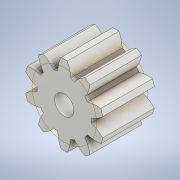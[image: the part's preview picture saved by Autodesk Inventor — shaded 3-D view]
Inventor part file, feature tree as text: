
AUTODESK INVENTOR PART (.ipt)
format: ipt  version: 2021 (Build 250183000, 183)  size: 220,160 bytes
history: native  units: mm (DEFAULTED — no unit token found)
features: plane x3, other x3, sketch x3, extrude x1, hole x1
ambient origin geometry x8: Origin, YZ Plane, XZ Plane, XY Plane, X Axis, Y Axis, Z Axis, Center Point
bodies: Solid1 (feature_tree)
feature tree (11):
  extrude  "Extrusion1"  Depth=8.0mm TaperAngle=0.0deg
  plane  "Work Plane2"
  plane  "Work Plane8"
  plane  "Work Plane9"
  other  "Spur Gear"
  hole  "Hole1"  [1 undecoded]
  sketch  "Sketch1"  dims[d0=12.303391mm d1=8.0mm d2=0.0mm]
  sketch  "Sketch2"  dims[d3=10.0mm d4=10.0mm d5=0.0mm]
  other  "Srf1"
  sketch  "Sketch3"  dims[d16=25.351695mm d17=0.0mm d34=3.141593mm d39=0.0mm d41=0.0mm d43=25.351695mm d46=25.351695mm d47=0.0mm d48=0.0mm d49=3.0mm d50=3.0mm d51=6.0mm d52=4.0mm d53=2.0mm d54=90.0deg d55=8.0mm d56=20.594885mm]
  other  "Pitch Diameter"
note: 1 required parameter value undecoded (feature->parameter linkage not recoverable at this tier; creation-order binding heuristic only, values carry confidence <= 0.55)
